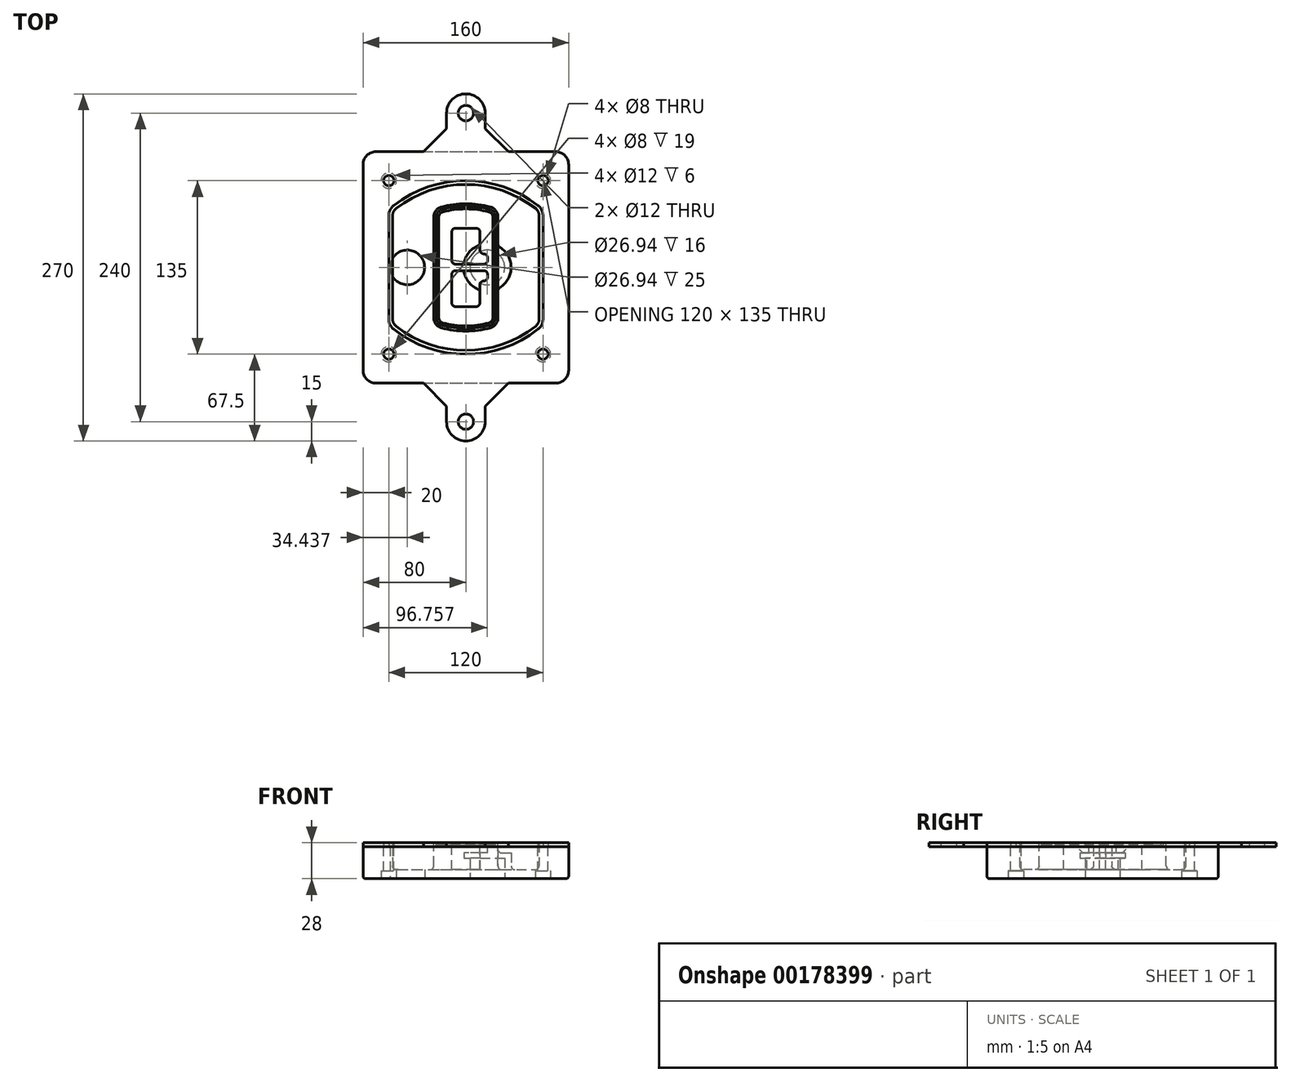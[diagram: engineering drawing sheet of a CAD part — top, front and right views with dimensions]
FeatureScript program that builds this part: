
annotation { "Feature Type Name" : "Feature", "Feature Type Description" : "" }
export const myFeature = defineFeature(function(context is Context, id is Id, definition is map)
    precondition{}
    {
        {
            var Q0;
            Q0=qCreatedBy(makeId("Top.planeOp"),FACE);
            var sketch = newSketch(context, id + "F0", { "sketchPlane" : qUnion([Q0])});
            skPoint(sketch, "E0.rect.middle", {"position": v(0, 0) * mm});
            skLineSegment(sketch, "E1.bottom", {"start": v(-70, -90) * mm, "end": v(70, -90) * mm});
            skLineSegment(sketch, "E1.top", {"start": v(-70, 90) * mm, "end": v(70, 90) * mm});
            skLineSegment(sketch, "E1.left", {"start": v(-80, -80) * mm, "end": v(-80, 80) * mm});
            skLineSegment(sketch, "E1.right", {"start": v(80, -80) * mm, "end": v(80, 80) * mm});
            skLineSegment(sketch, "E2", {"start": v(-80, 90) * mm, "end": v(80, -90) * mm, "construction": true});
            skLineSegment(sketch, "E3", {"start": v(80, 90) * mm, "end": v(-80, -90) * mm, "construction": true});
            skCircle(sketch, "E4", {"center": v(-60, 67.5) * mm, "radius": 4 * mm});
            skCircle(sketch, "E5", {"center": v(60, 67.5) * mm, "radius": 4 * mm});
            skCircle(sketch, "E6", {"center": v(60, -67.5) * mm, "radius": 4 * mm});
            skCircle(sketch, "E7", {"center": v(-60, -67.5) * mm, "radius": 4 * mm});
            skLineSegment(sketch, "E8", {"start": v(-60, 67.5) * mm, "end": v(60, 67.5) * mm, "construction": true});
            skLineSegment(sketch, "E9", {"start": v(60, 67.5) * mm, "end": v(60, -67.5) * mm, "construction": true});
            skLineSegment(sketch, "E10", {"start": v(60, -67.5) * mm, "end": v(-60, -67.5) * mm, "construction": true});
            skLineSegment(sketch, "E11", {"start": v(-60, -67.5) * mm, "end": v(-60, 67.5) * mm, "construction": true});
            skLineSegment(sketch, "E12", {"start": v(-60, 40.3) * mm, "end": v(-60, -40.3) * mm});
            skLineSegment(sketch, "E13", {"start": v(60, 40.3) * mm, "end": v(60, -40.3) * mm});
            skArc(sketch, "E14", {"start": v(56.15, 48.18) * mm, "mid": v(0, 67.5) * mm, "end": v(-56.15, 48.18) * mm});
            skArc(sketch, "E15", {"start": v(-56.15, -48.18) * mm, "mid": v(0, -67.5) * mm, "end": v(56.15, -48.18) * mm});
            skLineSegment(sketch, "E16", {"start": v(-60, 0) * mm, "end": v(60, 0) * mm, "construction": true});
            skPoint(sketch, "E17.visualSharp", {"position": v(-60, -45) * mm});
            skArc(sketch, "E17.filletArc", {"start": v(-60, -40.3) * mm, "mid": v(-58.99, -44.68) * mm, "end": v(-56.15, -48.18) * mm});
            skPoint(sketch, "E18.visualSharp", {"position": v(-60, 45) * mm});
            skArc(sketch, "E18.filletArc", {"start": v(-56.15, 48.18) * mm, "mid": v(-58.99, 44.68) * mm, "end": v(-60, 40.3) * mm});
            skPoint(sketch, "E19.visualSharp", {"position": v(60, 45) * mm});
            skArc(sketch, "E19.filletArc", {"start": v(60, 40.3) * mm, "mid": v(58.99, 44.68) * mm, "end": v(56.15, 48.18) * mm});
            skPoint(sketch, "E20.visualSharp", {"position": v(60, -45) * mm});
            skArc(sketch, "E20.filletArc", {"start": v(56.15, -48.18) * mm, "mid": v(58.99, -44.68) * mm, "end": v(60, -40.3) * mm});
            skPoint(sketch, "E21.visualSharp", {"position": v(-80, 90) * mm});
            skArc(sketch, "E21.filletArc", {"start": v(-70, 90) * mm, "mid": v(-77.07, 87.07) * mm, "end": v(-80, 80) * mm});
            skPoint(sketch, "E22.visualSharp", {"position": v(80, 90) * mm});
            skArc(sketch, "E22.filletArc", {"start": v(80, 80) * mm, "mid": v(77.07, 87.07) * mm, "end": v(70, 90) * mm});
            skPoint(sketch, "E23.visualSharp", {"position": v(80, -90) * mm});
            skArc(sketch, "E23.filletArc", {"start": v(70, -90) * mm, "mid": v(77.07, -87.07) * mm, "end": v(80, -80) * mm});
            skPoint(sketch, "E24.visualSharp", {"position": v(-80, -90) * mm});
            skArc(sketch, "E24.filletArc", {"start": v(-80, -80) * mm, "mid": v(-77.07, -87.07) * mm, "end": v(-70, -90) * mm});
            skArc(sketch, "E25.0", {"start": v(57, 40.3) * mm, "mid": v(56.3, 43.36) * mm, "end": v(54.3, 45.81) * mm});
            skLineSegment(sketch, "E25.1", {"start": v(57, 40.3) * mm, "end": v(57, -40.3) * mm});
            skArc(sketch, "E25.2", {"start": v(54.3, -45.81) * mm, "mid": v(56.3, -43.36) * mm, "end": v(57, -40.3) * mm});
            skArc(sketch, "E25.3", {"start": v(-54.3, -45.81) * mm, "mid": v(0, -64.5) * mm, "end": v(54.3, -45.81) * mm});
            skArc(sketch, "E25.4", {"start": v(-57, -40.3) * mm, "mid": v(-56.3, -43.36) * mm, "end": v(-54.3, -45.81) * mm});
            skArc(sketch, "E25.5", {"start": v(54.3, 45.81) * mm, "mid": v(0, 64.5) * mm, "end": v(-54.3, 45.81) * mm});
            skLineSegment(sketch, "E25.6", {"start": v(-57, 40.3) * mm, "end": v(-57, -40.3) * mm});
            skArc(sketch, "E25.7", {"start": v(-54.3, 45.81) * mm, "mid": v(-56.3, 43.36) * mm, "end": v(-57, 40.3) * mm});
            skArc(sketch, "E26.0", {"start": v(-58.62, 51.33) * mm, "mid": v(-62.58, 46.43) * mm, "end": v(-64, 40.3) * mm});
            skArc(sketch, "E26.1", {"start": v(58.62, 51.33) * mm, "mid": v(0, 71.5) * mm, "end": v(-58.62, 51.33) * mm});
            skArc(sketch, "E26.2", {"start": v(64, 40.3) * mm, "mid": v(62.58, 46.43) * mm, "end": v(58.62, 51.33) * mm});
            skLineSegment(sketch, "E26.3", {"start": v(64, 40.3) * mm, "end": v(64, -40.3) * mm});
            skArc(sketch, "E26.4", {"start": v(58.62, -51.33) * mm, "mid": v(62.58, -46.43) * mm, "end": v(64, -40.3) * mm});
            skLineSegment(sketch, "E26.5", {"start": v(-64, 40.3) * mm, "end": v(-64, -40.3) * mm});
            skArc(sketch, "E26.6", {"start": v(-58.62, -51.33) * mm, "mid": v(0, -71.5) * mm, "end": v(58.62, -51.33) * mm});
            skArc(sketch, "E26.7", {"start": v(-64, -40.3) * mm, "mid": v(-62.58, -46.43) * mm, "end": v(-58.62, -51.33) * mm});
            skSolve(sketch);
        }
        {
            var Q0;
            Q0=makeQuery(id+"F0.imprint","IMPRINT",FACE,{"disambiguationData":[TD([[makeQuery(id+"F0.imprint","IMPRINT",EDGE,{"derivedFrom":sQuery(id+"F0.wireOp",EDGE,"E1.bottom")}),1.0]])]});
            var Q1;
            Q1=makeQuery(id+"F0.imprint","IMPRINT",FACE,{"disambiguationData":[TD([[makeQuery(id+"F0.imprint","IMPRINT",EDGE,{"derivedFrom":sQuery(id+"F0.wireOp",EDGE,"E12")}),1.0]])]});
            var Q2;
            Q2=makeQuery(id+"F0.imprint","IMPRINT",FACE,{"disambiguationData":[TD([[makeQuery(id+"F0.imprint","IMPRINT",EDGE,{"derivedFrom":sQuery(id+"F0.wireOp",EDGE,"E25.0")}),1.0]])]});
            var Q3;
            Q3=makeQuery(id+"F0.imprint","IMPRINT",FACE,{"disambiguationData":[TD([[makeQuery(id+"F0.imprint","IMPRINT",EDGE,{"derivedFrom":sQuery(id+"F0.wireOp",EDGE,"E12")}),-1.0]])]});
            extrude(context, id + "F1", {"entities" : qUnion([Q0, Q1, Q2, Q3]), "oppositeDirection" : true, "depth" : 25 * mm});
        }
        {
            var Q0;
            Q0=makeQuery(id+"F0.imprint","IMPRINT",FACE,{"disambiguationData":[TD([[makeQuery(id+"F0.imprint","IMPRINT",EDGE,{"derivedFrom":sQuery(id+"F0.wireOp",EDGE,"E12")}),1.0]])]});
            extrude(context, id + "F2", {"entities" : qUnion([Q0]), "operationType" : NewBodyOperationType.ADD, "depth" : 3 * mm});
        }
        {
            var Q0;
            Q0=makeQuery(id+"F0.imprint","IMPRINT",FACE,{"disambiguationData":[TD([[makeQuery(id+"F0.imprint","IMPRINT",EDGE,{"derivedFrom":sQuery(id+"F0.wireOp",EDGE,"E25.0")}),1.0]])]});
            extrude(context, id + "F3", {"entities" : qUnion([Q0]), "operationType" : NewBodyOperationType.REMOVE, "oppositeDirection" : true, "depth" : 18 * mm});
        }
        {
            var Q0;
            Q0=makeQuery(id+"F2.opExtrude","CAP_FACE",FACE,{"disambiguationData":[OSD([sQuery(id+"F0.wireOp",EDGE,"E12"),sQuery(id+"F0.wireOp",EDGE,"E13"),sQuery(id+"F0.wireOp",EDGE,"E14"),sQuery(id+"F0.wireOp",EDGE,"E15"),sQuery(id+"F0.wireOp",EDGE,"E17.filletArc"),sQuery(id+"F0.wireOp",EDGE,"E18.filletArc"),sQuery(id+"F0.wireOp",EDGE,"E19.filletArc"),sQuery(id+"F0.wireOp",EDGE,"E20.filletArc"),sQuery(id+"F0.wireOp",EDGE,"E25.0"),sQuery(id+"F0.wireOp",EDGE,"E25.1"),sQuery(id+"F0.wireOp",EDGE,"E25.2"),sQuery(id+"F0.wireOp",EDGE,"E25.3"),sQuery(id+"F0.wireOp",EDGE,"E25.4"),sQuery(id+"F0.wireOp",EDGE,"E25.5"),sQuery(id+"F0.wireOp",EDGE,"E25.6"),sQuery(id+"F0.wireOp",EDGE,"E25.7")])],"isStart":false});
            var sketch = newSketch(context, id + "F4", { "sketchPlane" : qUnion([Q0])});
            skArc(sketch, "E27.0", {"start": v(-19.08, -46.97) * mm, "mid": v(0, -49.5) * mm, "end": v(19.08, -46.97) * mm});
            skArc(sketch, "E28.0", {"start": v(19.08, 46.97) * mm, "mid": v(0, 49.5) * mm, "end": v(-19.08, 46.97) * mm});
            skLineSegment(sketch, "E29", {"start": v(-25, 39.25) * mm, "end": v(-25, -39.25) * mm});
            skLineSegment(sketch, "E30", {"start": v(25, 39.25) * mm, "end": v(25, -39.25) * mm});
            skLineSegment(sketch, "E31", {"start": v(-25, 45.1) * mm, "end": v(25, 45.1) * mm, "construction": true});
            skLineSegment(sketch, "E32", {"start": v(-25, -45.1) * mm, "end": v(25, -45.1) * mm, "construction": true});
            skPoint(sketch, "E33.visualSharp", {"position": v(-25, 45.1) * mm});
            skArc(sketch, "E33.filletArc", {"start": v(-19.08, 46.97) * mm, "mid": v(-23.35, 44.11) * mm, "end": v(-25, 39.25) * mm});
            skPoint(sketch, "E34.visualSharp", {"position": v(25, 45.1) * mm});
            skArc(sketch, "E34.filletArc", {"start": v(25, 39.25) * mm, "mid": v(23.35, 44.11) * mm, "end": v(19.08, 46.97) * mm});
            skPoint(sketch, "E35.visualSharp", {"position": v(25, -45.1) * mm});
            skArc(sketch, "E35.filletArc", {"start": v(19.08, -46.97) * mm, "mid": v(23.35, -44.11) * mm, "end": v(25, -39.25) * mm});
            skPoint(sketch, "E36.visualSharp", {"position": v(-25, -45.1) * mm});
            skArc(sketch, "E36.filletArc", {"start": v(-25, -39.25) * mm, "mid": v(-23.35, -44.11) * mm, "end": v(-19.08, -46.97) * mm});
            skArc(sketch, "E37.0", {"start": v(54.3, 45.81) * mm, "mid": v(0, 64.5) * mm, "end": v(-54.3, 45.81) * mm});
            skArc(sketch, "E37.1", {"start": v(-54.3, 45.81) * mm, "mid": v(-56.3, 43.36) * mm, "end": v(-57, 40.3) * mm});
            skLineSegment(sketch, "E37.2", {"start": v(-57, 40.3) * mm, "end": v(-57, -40.3) * mm});
            skArc(sketch, "E37.3", {"start": v(-57, -40.3) * mm, "mid": v(-56.3, -43.36) * mm, "end": v(-54.3, -45.81) * mm});
            skArc(sketch, "E37.4", {"start": v(-54.3, -45.81) * mm, "mid": v(0, -64.5) * mm, "end": v(54.3, -45.81) * mm});
            skArc(sketch, "E37.5", {"start": v(54.3, -45.81) * mm, "mid": v(56.3, -43.36) * mm, "end": v(57, -40.3) * mm});
            skLineSegment(sketch, "E37.6", {"start": v(57, 40.3) * mm, "end": v(57, -40.3) * mm});
            skArc(sketch, "E37.7", {"start": v(57, 40.3) * mm, "mid": v(56.3, 43.36) * mm, "end": v(54.3, 45.81) * mm});
            skLineSegment(sketch, "E38.0", {"start": v(23, 39.25) * mm, "end": v(23, -39.25) * mm});
            skArc(sketch, "E38.1", {"start": v(18.56, -45.04) * mm, "mid": v(21.76, -42.9) * mm, "end": v(23, -39.25) * mm});
            skArc(sketch, "E38.2", {"start": v(-18.56, -45.04) * mm, "mid": v(0, -47.5) * mm, "end": v(18.56, -45.04) * mm});
            skArc(sketch, "E38.3", {"start": v(-23, -39.25) * mm, "mid": v(-21.76, -42.9) * mm, "end": v(-18.56, -45.04) * mm});
            skLineSegment(sketch, "E38.4", {"start": v(-23, 39.25) * mm, "end": v(-23, -39.25) * mm});
            skArc(sketch, "E38.5", {"start": v(23, 39.25) * mm, "mid": v(21.76, 42.9) * mm, "end": v(18.56, 45.04) * mm});
            skArc(sketch, "E38.6", {"start": v(-18.56, 45.04) * mm, "mid": v(-21.76, 42.9) * mm, "end": v(-23, 39.25) * mm});
            skArc(sketch, "E38.7", {"start": v(18.56, 45.04) * mm, "mid": v(0, 47.5) * mm, "end": v(-18.56, 45.04) * mm});
            skArc(sketch, "E39.0", {"start": v(21, 39.25) * mm, "mid": v(20.18, 41.68) * mm, "end": v(18.04, 43.1) * mm});
            skLineSegment(sketch, "E39.1", {"start": v(21, 39.25) * mm, "end": v(21, -39.25) * mm});
            skArc(sketch, "E39.2", {"start": v(18.04, -43.1) * mm, "mid": v(20.18, -41.68) * mm, "end": v(21, -39.25) * mm});
            skArc(sketch, "E39.3", {"start": v(-18.04, -43.1) * mm, "mid": v(0, -45.5) * mm, "end": v(18.04, -43.1) * mm});
            skArc(sketch, "E39.4", {"start": v(-21, -39.25) * mm, "mid": v(-20.18, -41.68) * mm, "end": v(-18.04, -43.1) * mm});
            skArc(sketch, "E39.5", {"start": v(18.04, 43.1) * mm, "mid": v(0, 45.5) * mm, "end": v(-18.04, 43.1) * mm});
            skLineSegment(sketch, "E39.6", {"start": v(-21, 39.25) * mm, "end": v(-21, -39.25) * mm});
            skArc(sketch, "E39.7", {"start": v(-18.04, 43.1) * mm, "mid": v(-20.18, 41.68) * mm, "end": v(-21, 39.25) * mm});
            skLineSegment(sketch, "E40", {"start": v(-25, 0) * mm, "end": v(25, 0) * mm, "construction": true});
            skLineSegment(sketch, "E41", {"start": v(-11, 5.5) * mm, "end": v(-11, 27.5) * mm});
            skLineSegment(sketch, "E42", {"start": v(-8, 30.5) * mm, "end": v(8, 30.5) * mm});
            skLineSegment(sketch, "E43", {"start": v(11, 27.5) * mm, "end": v(11, 13.5) * mm});
            skLineSegment(sketch, "E44", {"start": v(14, 10.5) * mm, "end": v(14, 10.5) * mm});
            skLineSegment(sketch, "E45", {"start": v(17, 7.5) * mm, "end": v(17, 5.5) * mm});
            skLineSegment(sketch, "E46", {"start": v(14, 2.5) * mm, "end": v(-8, 2.5) * mm});
            skPoint(sketch, "E47.visualSharp", {"position": v(-11, 30.5) * mm});
            skArc(sketch, "E47.filletArc", {"start": v(-8, 30.5) * mm, "mid": v(-10.12, 29.62) * mm, "end": v(-11, 27.5) * mm});
            skPoint(sketch, "E48.visualSharp", {"position": v(11, 30.5) * mm});
            skArc(sketch, "E48.filletArc", {"start": v(11, 27.5) * mm, "mid": v(10.12, 29.62) * mm, "end": v(8, 30.5) * mm});
            skPoint(sketch, "E49.visualSharp", {"position": v(11, 10.5) * mm});
            skArc(sketch, "E49.filletArc", {"start": v(11, 13.5) * mm, "mid": v(11.88, 11.38) * mm, "end": v(14, 10.5) * mm});
            skPoint(sketch, "E50.visualSharp", {"position": v(17, 10.5) * mm});
            skArc(sketch, "E50.filletArc", {"start": v(17, 7.5) * mm, "mid": v(16.12, 9.62) * mm, "end": v(14, 10.5) * mm});
            skPoint(sketch, "E51.visualSharp", {"position": v(17, 2.5) * mm});
            skArc(sketch, "E51.filletArc", {"start": v(14, 2.5) * mm, "mid": v(16.12, 3.38) * mm, "end": v(17, 5.5) * mm});
            skPoint(sketch, "E52.visualSharp", {"position": v(-11, 2.5) * mm});
            skArc(sketch, "E52.filletArc", {"start": v(-11, 5.5) * mm, "mid": v(-10.12, 3.38) * mm, "end": v(-8, 2.5) * mm});
            skLineSegment(sketch, "E53.0.MirrorCS", {"start": v(14, -2.5) * mm, "end": v(-8, -2.5) * mm});
            skArc(sketch, "E54.0.MirrorCS", {"start": v(-11, -5.5) * mm, "mid": v(-10.12, -3.38) * mm, "end": v(-8, -2.5) * mm});
            skLineSegment(sketch, "E55.0.MirrorCS", {"start": v(-11, -5.5) * mm, "end": v(-11, -27.5) * mm});
            skArc(sketch, "E56.0.MirrorCS", {"start": v(-8, -30.5) * mm, "mid": v(-10.12, -29.62) * mm, "end": v(-11, -27.5) * mm});
            skLineSegment(sketch, "E57.0.MirrorCS", {"start": v(-8, -30.5) * mm, "end": v(8, -30.5) * mm});
            skArc(sketch, "E58.0.MirrorCS", {"start": v(11, -27.5) * mm, "mid": v(10.12, -29.62) * mm, "end": v(8, -30.5) * mm});
            skLineSegment(sketch, "E59.0.MirrorCS", {"start": v(11, -27.5) * mm, "end": v(11, -13.5) * mm});
            skArc(sketch, "E60.0.MirrorCS", {"start": v(11, -13.5) * mm, "mid": v(11.88, -11.38) * mm, "end": v(14, -10.5) * mm});
            skArc(sketch, "E61.0.MirrorCS", {"start": v(17, -7.5) * mm, "mid": v(16.12, -9.62) * mm, "end": v(14, -10.5) * mm});
            skLineSegment(sketch, "E62.0.MirrorCS", {"start": v(17, -7.5) * mm, "end": v(17, -5.5) * mm});
            skArc(sketch, "E63.0.MirrorCS", {"start": v(14, -2.5) * mm, "mid": v(16.12, -3.38) * mm, "end": v(17, -5.5) * mm});
            skSolve(sketch);
        }
        {
            var Q0;
            Q0=makeQuery(id+"F4.imprint","IMPRINT",FACE,{"disambiguationData":[TD([[makeQuery(id+"F4.imprint","IMPRINT",EDGE,{"derivedFrom":sQuery(id+"F4.wireOp",EDGE,"E27.0")}),1.0]])]});
            var Q1;
            Q1=makeQuery(id+"F4.imprint","IMPRINT",FACE,{"disambiguationData":[TD([[makeQuery(id+"F4.imprint","IMPRINT",EDGE,{"derivedFrom":sQuery(id+"F4.wireOp",EDGE,"E38.0")}),-1.0]])]});
            var Q2;
            Q2=makeQuery(id+"F4.imprint","IMPRINT",FACE,{"disambiguationData":[TD([[makeQuery(id+"F4.imprint","IMPRINT",EDGE,{"derivedFrom":sQuery(id+"F4.wireOp",EDGE,"E39.0")}),1.0]])]});
            extrude(context, id + "F5", {"entities" : qUnion([Q0, Q1, Q2]), "operationType" : NewBodyOperationType.ADD, "endBound" : BoundingType.UP_TO_NEXT, "oppositeDirection" : true, "depth" : 25 * mm});
        }
        {
            var Q0;
            Q0=makeQuery(id+"F4.imprint","IMPRINT",FACE,{"disambiguationData":[TD([[makeQuery(id+"F4.imprint","IMPRINT",EDGE,{"derivedFrom":sQuery(id+"F4.wireOp",EDGE,"E38.0")}),-1.0]])]});
            extrude(context, id + "F6", {"entities" : qUnion([Q0]), "operationType" : NewBodyOperationType.REMOVE, "oppositeDirection" : true, "depth" : 2 * mm});
        }
        {
            var Q0;
            Q0=makeQuery(id+"F1.opExtrude","CAP_FACE",FACE,{"disambiguationData":[OSD([sQuery(id+"F0.wireOp",EDGE,"E1.bottom"),sQuery(id+"F0.wireOp",EDGE,"E1.top"),sQuery(id+"F0.wireOp",EDGE,"E1.left"),sQuery(id+"F0.wireOp",EDGE,"E1.right"),sQuery(id+"F0.wireOp",EDGE,"E4"),sQuery(id+"F0.wireOp",EDGE,"E5"),sQuery(id+"F0.wireOp",EDGE,"E6"),sQuery(id+"F0.wireOp",EDGE,"E7"),sQuery(id+"F0.wireOp",EDGE,"E21.filletArc"),sQuery(id+"F0.wireOp",EDGE,"E22.filletArc"),sQuery(id+"F0.wireOp",EDGE,"E23.filletArc"),sQuery(id+"F0.wireOp",EDGE,"E24.filletArc")])],"isStart":false});
            var sketch = newSketch(context, id + "F7", { "sketchPlane" : qUnion([Q0])});
            skCircle(sketch, "E64", {"center": v(16.76, 0) * mm, "radius": 13.47 * mm});
            skCircle(sketch, "E65", {"center": v(-45.56, 0) * mm, "radius": 13.47 * mm});
            skLineSegment(sketch, "E66", {"start": v(80, 0) * mm, "end": v(-80, 0) * mm});
            skCircle(sketch, "E67", {"center": v(16.76, 0) * mm, "radius": 18.47 * mm});
            skCircle(sketch, "E68", {"center": v(60, -67.5) * mm, "radius": 6 * mm});
            skCircle(sketch, "E69", {"center": v(-60, -67.5) * mm, "radius": 6 * mm});
            skCircle(sketch, "E70", {"center": v(-60, 67.5) * mm, "radius": 6 * mm});
            skCircle(sketch, "E71", {"center": v(60, 67.5) * mm, "radius": 6 * mm});
            skSolve(sketch);
        }
        {
            var Q0;
            {var subQ1=sQuery(id+"F7.wireOp",EDGE,"E66");var subQ4=sQuery(id+"F7.wireOp",EDGE,"E64");var subQ6=makeQuery(id+"F7.imprint","INTERSECT",VERTEX,{"disambiguationData":[OD(0.0)],"derivedFrom":[subQ4,subQ1]});Q0=makeQuery(id+"F7.imprint","IMPRINT",FACE,{"disambiguationData":[TD([[makeQuery(id+"F7.imprint","IMPRINT",EDGE,{"disambiguationData":[TD([[subQ6,-1.0]])],"derivedFrom":subQ4}),-1.0]])]});}
            var Q1;
            {var subQ0=sQuery(id+"F7.wireOp",EDGE,"E66");var subQ1=sQuery(id+"F7.wireOp",EDGE,"E64");var subQ3=makeQuery(id+"F7.imprint","INTERSECT",VERTEX,{"disambiguationData":[OD(0.0)],"derivedFrom":[subQ1,subQ0]});Q1=makeQuery(id+"F7.imprint","IMPRINT",FACE,{"disambiguationData":[TD([[makeQuery(id+"F7.imprint","IMPRINT",EDGE,{"disambiguationData":[TD([[subQ3,-1.0]])],"derivedFrom":subQ1}),1.0]])]});}
            var Q2;
            {var subQ0=sQuery(id+"F7.wireOp",EDGE,"E66");var subQ1=sQuery(id+"F7.wireOp",EDGE,"E64");var subQ3=makeQuery(id+"F7.imprint","INTERSECT",VERTEX,{"disambiguationData":[OD(0.0)],"derivedFrom":[subQ1,subQ0]});Q2=makeQuery(id+"F7.imprint","IMPRINT",FACE,{"disambiguationData":[TD([[makeQuery(id+"F7.imprint","IMPRINT",EDGE,{"disambiguationData":[TD([[subQ3,1.0]])],"derivedFrom":subQ1}),1.0]])]});}
            var Q3;
            {var subQ1=sQuery(id+"F7.wireOp",EDGE,"E66");var subQ4=sQuery(id+"F7.wireOp",EDGE,"E64");var subQ6=makeQuery(id+"F7.imprint","INTERSECT",VERTEX,{"disambiguationData":[OD(0.0)],"derivedFrom":[subQ4,subQ1]});Q3=makeQuery(id+"F7.imprint","IMPRINT",FACE,{"disambiguationData":[TD([[makeQuery(id+"F7.imprint","IMPRINT",EDGE,{"disambiguationData":[TD([[subQ6,1.0]])],"derivedFrom":subQ4}),-1.0]])]});}
            extrude(context, id + "F8", {"entities" : qUnion([Q0, Q1, Q2, Q3]), "operationType" : NewBodyOperationType.ADD, "oppositeDirection" : true, "depth" : 20 * mm});
        }
        {
            var Q0;
            {var subQ0=sQuery(id+"F7.wireOp",EDGE,"E66");var subQ1=sQuery(id+"F7.wireOp",EDGE,"E64");var subQ3=makeQuery(id+"F7.imprint","INTERSECT",VERTEX,{"disambiguationData":[OD(0.0)],"derivedFrom":[subQ1,subQ0]});Q0=makeQuery(id+"F7.imprint","IMPRINT",FACE,{"disambiguationData":[TD([[makeQuery(id+"F7.imprint","IMPRINT",EDGE,{"disambiguationData":[TD([[subQ3,-1.0]])],"derivedFrom":subQ1}),1.0]])]});}
            var Q1;
            {var subQ0=sQuery(id+"F7.wireOp",EDGE,"E66");var subQ1=sQuery(id+"F7.wireOp",EDGE,"E64");var subQ3=makeQuery(id+"F7.imprint","INTERSECT",VERTEX,{"disambiguationData":[OD(0.0)],"derivedFrom":[subQ1,subQ0]});Q1=makeQuery(id+"F7.imprint","IMPRINT",FACE,{"disambiguationData":[TD([[makeQuery(id+"F7.imprint","IMPRINT",EDGE,{"disambiguationData":[TD([[subQ3,1.0]])],"derivedFrom":subQ1}),1.0]])]});}
            extrude(context, id + "F9", {"entities" : qUnion([Q0, Q1]), "operationType" : NewBodyOperationType.REMOVE, "oppositeDirection" : true, "depth" : 16 * mm});
        }
        {
            var Q0;
            {var subQ0=sQuery(id+"F7.wireOp",EDGE,"E66");var subQ1=sQuery(id+"F7.wireOp",EDGE,"E65");var subQ3=makeQuery(id+"F7.imprint","INTERSECT",VERTEX,{"disambiguationData":[OD(0.0)],"derivedFrom":[subQ1,subQ0]});Q0=makeQuery(id+"F7.imprint","IMPRINT",FACE,{"disambiguationData":[TD([[makeQuery(id+"F7.imprint","IMPRINT",EDGE,{"disambiguationData":[TD([[subQ3,-1.0]])],"derivedFrom":subQ1}),1.0]])]});}
            var Q1;
            {var subQ0=sQuery(id+"F7.wireOp",EDGE,"E66");var subQ1=sQuery(id+"F7.wireOp",EDGE,"E65");var subQ3=makeQuery(id+"F7.imprint","INTERSECT",VERTEX,{"disambiguationData":[OD(0.0)],"derivedFrom":[subQ1,subQ0]});Q1=makeQuery(id+"F7.imprint","IMPRINT",FACE,{"disambiguationData":[TD([[makeQuery(id+"F7.imprint","IMPRINT",EDGE,{"disambiguationData":[TD([[subQ3,1.0]])],"derivedFrom":subQ1}),1.0]])]});}
            extrude(context, id + "F10", {"entities" : qUnion([Q0, Q1]), "operationType" : NewBodyOperationType.REMOVE, "oppositeDirection" : true, "depth" : 25 * mm});
        }
        {
            var Q0;
            Q0=makeQuery(id+"F7.imprint","IMPRINT",FACE,{"disambiguationData":[TD([[makeQuery(id+"F7.imprint","IMPRINT",EDGE,{"derivedFrom":sQuery(id+"F7.wireOp",EDGE,"E68")}),1.0]])]});
            var Q1;
            Q1=makeQuery(id+"F7.imprint","IMPRINT",FACE,{"disambiguationData":[TD([[makeQuery(id+"F7.imprint","IMPRINT",EDGE,{"derivedFrom":makeQuery(id+"F1.opExtrude","CAP_EDGE",EDGE,{"disambiguationData":[OSD([sQuery(id+"F0.wireOp",EDGE,"E5")])],"isStart":false})}),-1.0]])]});
            var Q2;
            Q2=makeQuery(id+"F7.imprint","IMPRINT",FACE,{"disambiguationData":[TD([[makeQuery(id+"F7.imprint","IMPRINT",EDGE,{"derivedFrom":sQuery(id+"F7.wireOp",EDGE,"E69")}),1.0]])]});
            var Q3;
            Q3=makeQuery(id+"F7.imprint","IMPRINT",FACE,{"disambiguationData":[TD([[makeQuery(id+"F7.imprint","IMPRINT",EDGE,{"derivedFrom":makeQuery(id+"F1.opExtrude","CAP_EDGE",EDGE,{"disambiguationData":[OSD([sQuery(id+"F0.wireOp",EDGE,"E4")])],"isStart":false})}),-1.0]])]});
            var Q4;
            Q4=makeQuery(id+"F7.imprint","IMPRINT",FACE,{"disambiguationData":[TD([[makeQuery(id+"F7.imprint","IMPRINT",EDGE,{"derivedFrom":sQuery(id+"F7.wireOp",EDGE,"E70")}),1.0]])]});
            var Q5;
            Q5=makeQuery(id+"F7.imprint","IMPRINT",FACE,{"disambiguationData":[TD([[makeQuery(id+"F7.imprint","IMPRINT",EDGE,{"derivedFrom":makeQuery(id+"F1.opExtrude","CAP_EDGE",EDGE,{"disambiguationData":[OSD([sQuery(id+"F0.wireOp",EDGE,"E7")])],"isStart":false})}),-1.0]])]});
            var Q6;
            Q6=makeQuery(id+"F7.imprint","IMPRINT",FACE,{"disambiguationData":[TD([[makeQuery(id+"F7.imprint","IMPRINT",EDGE,{"derivedFrom":sQuery(id+"F7.wireOp",EDGE,"E71")}),1.0]])]});
            var Q7;
            Q7=makeQuery(id+"F7.imprint","IMPRINT",FACE,{"disambiguationData":[TD([[makeQuery(id+"F7.imprint","IMPRINT",EDGE,{"derivedFrom":makeQuery(id+"F1.opExtrude","CAP_EDGE",EDGE,{"disambiguationData":[OSD([sQuery(id+"F0.wireOp",EDGE,"E6")])],"isStart":false})}),-1.0]])]});
            extrude(context, id + "F11", {"entities" : qUnion([Q0, Q1, Q2, Q3, Q4, Q5, Q6, Q7]), "operationType" : NewBodyOperationType.REMOVE, "oppositeDirection" : true, "depth" : 6 * mm});
        }
        {
            var Q0;
            Q0=makeQuery(id+"F9.boolean.opBoolean","COPY",FACE,{"derivedFrom":makeQuery(id+"F9.opExtrude","CAP_FACE",FACE,{"disambiguationData":[OSD([sQuery(id+"F7.wireOp",EDGE,"E64")])],"isStart":false})});
            var sketch = newSketch(context, id + "F12", { "sketchPlane" : qUnion([Q0])});
            skArc(sketch, "E72.0", {"start": v(11, 17.55) * mm, "mid": v(2.57, 11.82) * mm, "end": v(-1.54, 2.5) * mm});
            skArc(sketch, "E72.1", {"start": v(-1.54, -2.5) * mm, "mid": v(2.57, -11.82) * mm, "end": v(11, -17.55) * mm});
            skLineSegment(sketch, "E73", {"start": v(-1.54, -2.5) * mm, "end": v(14, -2.5) * mm});
            skLineSegment(sketch, "E74.0", {"start": v(14, 2.5) * mm, "end": v(-1.54, 2.5) * mm});
            skArc(sketch, "E74.1", {"start": v(14, 2.5) * mm, "mid": v(16.12, 3.38) * mm, "end": v(17, 5.5) * mm});
            skLineSegment(sketch, "E74.2", {"start": v(17, 7.5) * mm, "end": v(17, 5.5) * mm});
            skArc(sketch, "E74.3", {"start": v(17, 7.5) * mm, "mid": v(16.12, 9.62) * mm, "end": v(14, 10.5) * mm});
            skArc(sketch, "E74.4", {"start": v(11, 13.5) * mm, "mid": v(11.88, 11.38) * mm, "end": v(14, 10.5) * mm});
            skLineSegment(sketch, "E74.5", {"start": v(11, 17.55) * mm, "end": v(11, 13.5) * mm});
            skLineSegment(sketch, "E74.7", {"start": v(14, -2.5) * mm, "end": v(-1.54, -2.5) * mm});
            skArc(sketch, "E74.8", {"start": v(14, -2.5) * mm, "mid": v(16.12, -3.38) * mm, "end": v(17, -5.5) * mm});
            skLineSegment(sketch, "E74.9", {"start": v(17, -7.5) * mm, "end": v(17, -5.5) * mm});
            skArc(sketch, "E74.10", {"start": v(17, -7.5) * mm, "mid": v(16.12, -9.62) * mm, "end": v(14, -10.5) * mm});
            skArc(sketch, "E74.11", {"start": v(11, -13.5) * mm, "mid": v(11.88, -11.38) * mm, "end": v(14, -10.5) * mm});
            skLineSegment(sketch, "E74.12", {"start": v(11, -17.55) * mm, "end": v(11, -13.5) * mm});
            skPoint(sketch, "E75.orphan", {"position": v(11, -27.5) * mm});
            skPoint(sketch, "E76.orphan", {"position": v(-8, -2.5) * mm});
            skPoint(sketch, "E77.orphan", {"position": v(-8, 2.5) * mm});
            skPoint(sketch, "E78.orphan", {"position": v(11, 27.5) * mm});
            skSolve(sketch);
        }
        {
            var Q0;
            {var subQ7=sQuery(id+"F12.wireOp",EDGE,"E72.0");var subQ14=sQuery(id+"F12.wireOp",EDGE,"E72.1");var subQ16=sQuery(id+"F12.wireOp",EDGE,"E74.1");var subQ18=sQuery(id+"F12.wireOp",EDGE,"E74.8");Q0=qUnion([makeQuery(id+"F12.imprint","IMPRINT",FACE,{"disambiguationData":[TD([[makeQuery(id+"F12.imprint","IMPRINT",EDGE,{"derivedFrom":subQ7}),1.0]])]}),makeQuery(id+"F12.imprint","IMPRINT",FACE,{"disambiguationData":[TD([[makeQuery(id+"F12.imprint","IMPRINT",EDGE,{"derivedFrom":subQ14}),1.0]])]}),makeQuery(id+"F12.imprint","IMPRINT",FACE,{"disambiguationData":[TD([[makeQuery(id+"F12.imprint","IMPRINT",EDGE,{"derivedFrom":subQ16}),1.0]])]}),makeQuery(id+"F12.imprint","IMPRINT",FACE,{"disambiguationData":[TD([[makeQuery(id+"F12.imprint","IMPRINT",EDGE,{"derivedFrom":subQ18}),-1.0]])]})]);}
            var Q1;
            Q1=makeQuery(id+"F5.boolean.opBoolean","SPLIT",FACE,{"disambiguationData":[TD([makeQuery(id+"F5.opExtrude","SWEPT_FACE",FACE,{"disambiguationData":[OSD([sQuery(id+"F4.wireOp",EDGE,"E41")])]})])],"derivedFrom":makeQuery(id+"F3.boolean.opBoolean","COPY",FACE,{"derivedFrom":makeQuery(id+"F3.opExtrude","CAP_FACE",FACE,{"disambiguationData":[OSD([sQuery(id+"F0.wireOp",EDGE,"E25.0"),sQuery(id+"F0.wireOp",EDGE,"E25.1"),sQuery(id+"F0.wireOp",EDGE,"E25.2"),sQuery(id+"F0.wireOp",EDGE,"E25.3"),sQuery(id+"F0.wireOp",EDGE,"E25.4"),sQuery(id+"F0.wireOp",EDGE,"E25.5"),sQuery(id+"F0.wireOp",EDGE,"E25.6"),sQuery(id+"F0.wireOp",EDGE,"E25.7")])],"isStart":false})})});
            extrude(context, id + "F13", {"entities" : qUnion([Q0]), "operationType" : NewBodyOperationType.REMOVE, "endBound" : BoundingType.UP_TO_SURFACE, "endBoundEntityFace" : qUnion([Q1]), "depth" : 25 * mm});
        }
        {
            var Q0;
            Q0=makeQuery(id+"F3.boolean.opBoolean","COPY",EDGE,{"derivedFrom":makeQuery(id+"F3.opExtrude","CAP_EDGE",EDGE,{"disambiguationData":[OSD([sQuery(id+"F0.wireOp",EDGE,"E25.6")])],"isStart":false})});
            var Q1;
            Q1=makeQuery(id+"F8.boolean.opBoolean","INTERSECT",EDGE,{"derivedFrom":[makeQuery(id+"F5.opExtrude","SWEPT_FACE",FACE,{"disambiguationData":[OSD([sQuery(id+"F4.wireOp",EDGE,"E30")])]}),makeQuery(id+"F8.opExtrude","CAP_FACE",FACE,{"disambiguationData":[OSD([sQuery(id+"F7.wireOp",EDGE,"E67")])],"isStart":false})]});
            var Q2;
            Q2=makeQuery(id+"F8.boolean.opBoolean","INTERSECT",EDGE,{"disambiguationData":[OD(1.0)],"derivedFrom":[makeQuery(id+"F5.opExtrude","SWEPT_FACE",FACE,{"disambiguationData":[OSD([sQuery(id+"F4.wireOp",EDGE,"E30")])]}),makeQuery(id+"F8.opExtrude","SWEPT_FACE",FACE,{"disambiguationData":[OSD([sQuery(id+"F7.wireOp",EDGE,"E67")])]})]});
            var Q3;
            {var subQ0=sQuery(id+"F4.wireOp",EDGE,"E30");Q3=makeQuery(id+"F8.boolean.opBoolean","SPLIT",EDGE,{"disambiguationData":[TD([makeQuery(id+"F5.opExtrude","SWEPT_FACE",FACE,{"disambiguationData":[OSD([sQuery(id+"F4.wireOp",EDGE,"E35.filletArc")])]})])],"derivedFrom":makeQuery(id+"F5.opExtrude","CAP_EDGE",EDGE,{"disambiguationData":[OSD([subQ0])],"isStart":false})});}
            var Q4;
            {var subQ0=sQuery(id+"F0.wireOp",EDGE,"E25.7");var subQ1=sQuery(id+"F0.wireOp",EDGE,"E25.1");var subQ2=sQuery(id+"F0.wireOp",EDGE,"E25.6");var subQ3=sQuery(id+"F0.wireOp",EDGE,"E25.5");var subQ4=sQuery(id+"F0.wireOp",EDGE,"E25.4");var subQ5=sQuery(id+"F0.wireOp",EDGE,"E25.0");var subQ6=sQuery(id+"F0.wireOp",EDGE,"E25.2");var subQ7=sQuery(id+"F0.wireOp",EDGE,"E25.3");Q4=makeQuery(id+"F8.boolean.opBoolean","INTERSECT",EDGE,{"derivedFrom":[makeQuery(id+"F5.boolean.opBoolean","SPLIT",FACE,{"disambiguationData":[TD([makeQuery(id+"F2.opExtrude","SWEPT_FACE",FACE,{"disambiguationData":[OSD([subQ5])]})])],"derivedFrom":makeQuery(id+"F3.boolean.opBoolean","COPY",FACE,{"derivedFrom":makeQuery(id+"F3.opExtrude","CAP_FACE",FACE,{"disambiguationData":[OSD([subQ5,subQ1,subQ6,subQ7,subQ4,subQ3,subQ2,subQ0])],"isStart":false})})}),makeQuery(id+"F8.opExtrude","SWEPT_FACE",FACE,{"disambiguationData":[OSD([sQuery(id+"F7.wireOp",EDGE,"E67")])]})]});}
            var Q5;
            Q5=makeQuery(id+"F8.boolean.opBoolean","INTERSECT",EDGE,{"disambiguationData":[OD(0.0)],"derivedFrom":[makeQuery(id+"F5.opExtrude","SWEPT_FACE",FACE,{"disambiguationData":[OSD([sQuery(id+"F4.wireOp",EDGE,"E30")])]}),makeQuery(id+"F8.opExtrude","SWEPT_FACE",FACE,{"disambiguationData":[OSD([sQuery(id+"F7.wireOp",EDGE,"E67")])]})]});
            fillet(context, id + "F14", {"entities" : qUnion([Q0, Q1, Q2, Q3, Q4, Q5]), "radius" : 3 * mm, "tangentPropagation" : true, "allowEdgeOverflow" : false});
        }
        {
            var Q0;
            Q0=makeQuery(id+"F1.opExtrude","CAP_EDGE",EDGE,{"disambiguationData":[OSD([sQuery(id+"F0.wireOp",EDGE,"E1.bottom")])],"isStart":false});
            fillet(context, id + "F15", {"entities" : qUnion([Q0]), "radius" : 2 * mm, "tangentPropagation" : true, "allowEdgeOverflow" : false});
        }
        {
            var Q0;
            {var subQ0=sQuery(id+"F0.wireOp",EDGE,"E22.filletArc");var subQ1=sQuery(id+"F0.wireOp",EDGE,"E7");var subQ2=sQuery(id+"F0.wireOp",EDGE,"E6");var subQ3=sQuery(id+"F0.wireOp",EDGE,"E5");var subQ4=sQuery(id+"F0.wireOp",EDGE,"E4");var subQ5=sQuery(id+"F0.wireOp",EDGE,"E1.bottom");var subQ6=sQuery(id+"F0.wireOp",EDGE,"E21.filletArc");var subQ7=sQuery(id+"F0.wireOp",EDGE,"E1.top");var subQ8=sQuery(id+"F0.wireOp",EDGE,"E1.left");var subQ9=sQuery(id+"F0.wireOp",EDGE,"E1.right");var subQ10=sQuery(id+"F0.wireOp",EDGE,"E23.filletArc");var subQ11=sQuery(id+"F0.wireOp",EDGE,"E24.filletArc");Q0=makeQuery(id+"F2.boolean.opBoolean","SPLIT",FACE,{"disambiguationData":[TD([makeQuery(id+"F1.opExtrude","SWEPT_FACE",FACE,{"disambiguationData":[OSD([subQ5])]})])],"derivedFrom":makeQuery(id+"F1.opExtrude","CAP_FACE",FACE,{"disambiguationData":[OSD([subQ5,subQ7,subQ8,subQ9,subQ4,subQ3,subQ2,subQ1,subQ6,subQ0,subQ10,subQ11])],"isStart":true})});}
            var sketch = newSketch(context, id + "F16", { "sketchPlane" : qUnion([Q0])});
            skLineSegment(sketch, "E79", {"start": v(-33, 90) * mm, "end": v(-15, 108) * mm});
            skLineSegment(sketch, "E80", {"start": v(-15, 108) * mm, "end": v(-15, 120) * mm});
            skLineSegment(sketch, "E81", {"start": v(15, 120) * mm, "end": v(15, 108) * mm});
            skLineSegment(sketch, "E82", {"start": v(15, 108) * mm, "end": v(33, 90) * mm});
            skLineSegment(sketch, "E83", {"start": v(0, 120) * mm, "end": v(0, 90) * mm, "construction": true});
            skArc(sketch, "E84", {"start": v(-15, 120) * mm, "mid": v(0, 135) * mm, "end": v(15, 120) * mm});
            skCircle(sketch, "E85", {"center": v(0, 120) * mm, "radius": 6 * mm});
            skLineSegment(sketch, "E86", {"start": v(-80, 0) * mm, "end": v(80, 0) * mm, "construction": true});
            skLineSegment(sketch, "E87.MirrorCS", {"start": v(15, -120) * mm, "end": v(15, -108) * mm});
            skLineSegment(sketch, "E88.MirrorCS", {"start": v(-33, -90) * mm, "end": v(-15, -108) * mm});
            skLineSegment(sketch, "E89.MirrorCS", {"start": v(15, -108) * mm, "end": v(33, -90) * mm});
            skLineSegment(sketch, "E90.MirrorCS", {"start": v(-15, -108) * mm, "end": v(-15, -120) * mm});
            skLineSegment(sketch, "E91.MirrorCS", {"start": v(0, -120) * mm, "end": v(0, -90) * mm, "construction": true});
            skCircle(sketch, "E92.MirrorC", {"center": v(0, -120) * mm, "radius": 6 * mm});
            skArc(sketch, "E93.MirrorCS", {"start": v(-15, -120) * mm, "mid": v(0, -135) * mm, "end": v(15, -120) * mm});
            skSolve(sketch);
        }
        {
            var Q0;
            {var subQ1=sQuery(id+"F16.wireOp",EDGE,"E79");Q0=makeQuery(id+"F16.imprint","IMPRINT",FACE,{"disambiguationData":[TD([[makeQuery(id+"F16.imprint","IMPRINT",EDGE,{"derivedFrom":subQ1}),-1.0]])]});}
            var Q1;
            Q1=makeQuery(id+"F16.imprint","IMPRINT",FACE,{"disambiguationData":[TD([[makeQuery(id+"F16.imprint","IMPRINT",EDGE,{"derivedFrom":makeQuery(id+"F1.opExtrude","CAP_EDGE",EDGE,{"disambiguationData":[OSD([sQuery(id+"F0.wireOp",EDGE,"E1.left")])],"isStart":true})}),-1.0]])]});
            var Q2;
            Q2=makeQuery(id+"F16.imprint","IMPRINT",FACE,{"disambiguationData":[TD([[makeQuery(id+"F16.imprint","IMPRINT",EDGE,{"derivedFrom":sQuery(id+"F16.wireOp",EDGE,"E87.MirrorCS")}),1.0]])]});
            var Q3;
            Q3=makeQuery(id+"F2.opExtrude","CAP_FACE",FACE,{"disambiguationData":[OSD([sQuery(id+"F0.wireOp",EDGE,"E12"),sQuery(id+"F0.wireOp",EDGE,"E13"),sQuery(id+"F0.wireOp",EDGE,"E14"),sQuery(id+"F0.wireOp",EDGE,"E15"),sQuery(id+"F0.wireOp",EDGE,"E17.filletArc"),sQuery(id+"F0.wireOp",EDGE,"E18.filletArc"),sQuery(id+"F0.wireOp",EDGE,"E19.filletArc"),sQuery(id+"F0.wireOp",EDGE,"E20.filletArc"),sQuery(id+"F0.wireOp",EDGE,"E25.0"),sQuery(id+"F0.wireOp",EDGE,"E25.1"),sQuery(id+"F0.wireOp",EDGE,"E25.2"),sQuery(id+"F0.wireOp",EDGE,"E25.3"),sQuery(id+"F0.wireOp",EDGE,"E25.4"),sQuery(id+"F0.wireOp",EDGE,"E25.5"),sQuery(id+"F0.wireOp",EDGE,"E25.6"),sQuery(id+"F0.wireOp",EDGE,"E25.7")])],"isStart":false});
            extrude(context, id + "F17", {"entities" : qUnion([Q0, Q1, Q2]), "endBound" : BoundingType.UP_TO_SURFACE, "endBoundEntityFace" : qUnion([Q3]), "depth" : 25 * mm});
        }
    });
